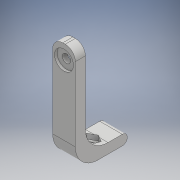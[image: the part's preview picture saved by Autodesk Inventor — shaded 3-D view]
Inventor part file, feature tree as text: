
AUTODESK INVENTOR PART (.ipt)
format: ipt  version: 2019 (Build 230136000, 136)  size: 226,304 bytes
history: native  units: mm
features: extrude x11, sketch x11, fillet x4, other x1, projected_geometry x1
ambient origin geometry x8: Origin, YZ Plane, XZ Plane, XY Plane, X Axis, Y Axis, Z Axis, Center Point
bodies: Body1 (feature_tree)
feature tree (28):
  other  "Sólido1"
  extrude  "Extrusión1"  Depth=6.0mm TaperAngle=0.0deg
  extrude  "Extrusión2"  Depth=115.0mm TaperAngle=0.0deg
  extrude  "Extrusión3"  Depth=11.0mm
  extrude  "Extrusión4"  Depth=27.0mm
  extrude  "Extrusión8"  Depth=12.0mm
  extrude  "Extrusión9"  Depth=10.0mm TaperAngle=0.0deg
  extrude  "Extrusión10"  Depth=2.5mm TaperAngle=0.0deg
  extrude  "Extrusión11"  Depth=3.0mm TaperAngle=0.0deg
  extrude  "Extrusión12"  Depth=10.0mm
  extrude  "Extrusión13"  Depth=24.0mm
  fillet  "Empalme4"  Radius=8.0mm
  extrude  "Extrusión14"  Depth=27.0mm
  fillet  "Empalme7"  Radius=10.0mm
  fillet  "Empalme8"  Radius=6.0mm
  fillet  "Empalme9"  Radius=27.0mm
  sketch  "Boceto1"  dims[d0=6.0mm d1=0.0mm d2=6.0mm d3=0.0mm]
  sketch  "Boceto2"  dims[d5=3.0mm d6=0.0mm d7=115.0mm d8=0.0mm]
  projected_geometry  "Contorno proyectado1"
  sketch  "Boceto3"  dims[d18=11.0mm d20=17.0mm]
  sketch  "Boceto5"  dims[d21=5.0mm d22=27.0mm]
  sketch  "Boceto9"  dims[d23=62.0mm d24=12.0mm]
  sketch  "Boceto10"  dims[d25=10.0mm d26=10.0mm d27=0.0mm]
  sketch  "Boceto11"  dims[d29=22.0mm d30=2.5mm d31=0.0mm]
  sketch  "Boceto12"  dims[d32=12.0mm d34=3.0mm d35=0.0mm]
  sketch  "Boceto14"  dims[d36=3.0mm d37=0.0mm d38=10.0mm]
  sketch  "Boceto15"  dims[d39=3.0mm d40=0.0mm d41=24.0mm d42=8.0mm d43=0.0mm]
  sketch  "Boceto17"  dims[d45=16.0mm d46=12.0mm d49=10.0mm d50=0.0mm d51=6.0mm d52=27.0mm d53=27.0mm]
